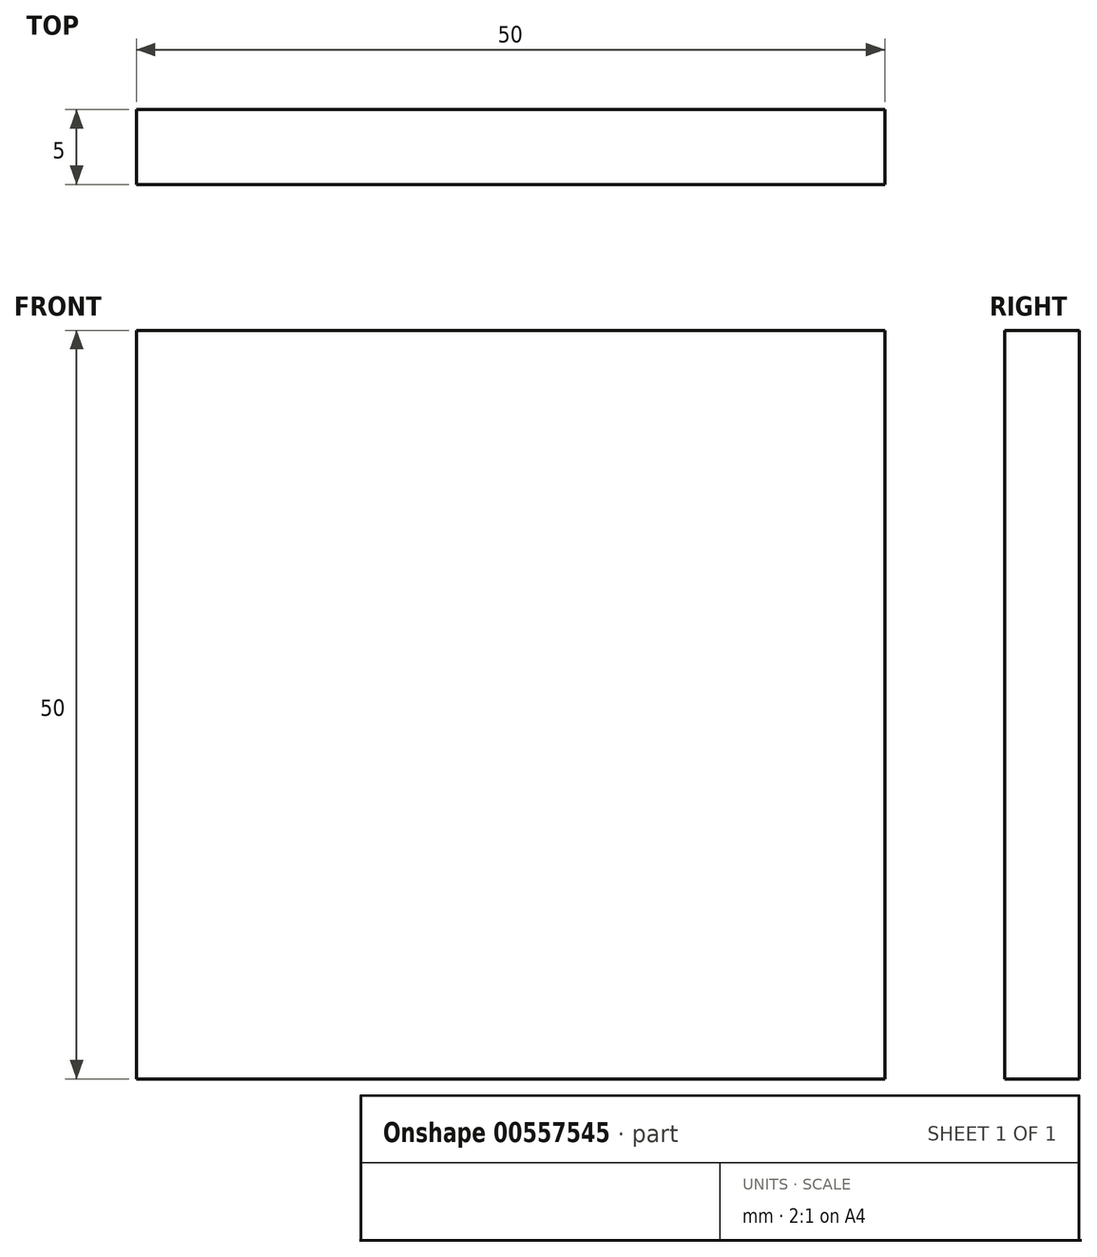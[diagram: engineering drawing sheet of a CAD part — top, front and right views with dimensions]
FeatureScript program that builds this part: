
annotation { "Feature Type Name" : "Feature", "Feature Type Description" : "" }
export const myFeature = defineFeature(function(context is Context, id is Id, definition is map)
    precondition{}
    {
        {
            var Q0;
            Q0=qCreatedBy(makeId("Front.planeOp"),FACE);
            var sketch = newSketch(context, id + "F0", { "sketchPlane" : qUnion([Q0])});
            skLineSegment(sketch, "E0.bottom", {"start": v(25, 25) * mm, "end": v(-25, 25) * mm});
            skLineSegment(sketch, "E0.top", {"start": v(25, -25) * mm, "end": v(-25, -25) * mm});
            skLineSegment(sketch, "E0.left", {"start": v(25, 25) * mm, "end": v(25, -25) * mm});
            skLineSegment(sketch, "E0.right", {"start": v(-25, 25) * mm, "end": v(-25, -25) * mm});
            skPoint(sketch, "E0.middle", {"position": v(0, 0) * mm});
            skSolve(sketch);
        }
        {
            var Q0;
            Q0 = qSketchRegion(id + "F0", true);
            extrude(context, id + "F1", {"entities" : qUnion([Q0]), "depth" : 5 * mm, "offsetDistance" : 25.4 * mm});
        }
    });
